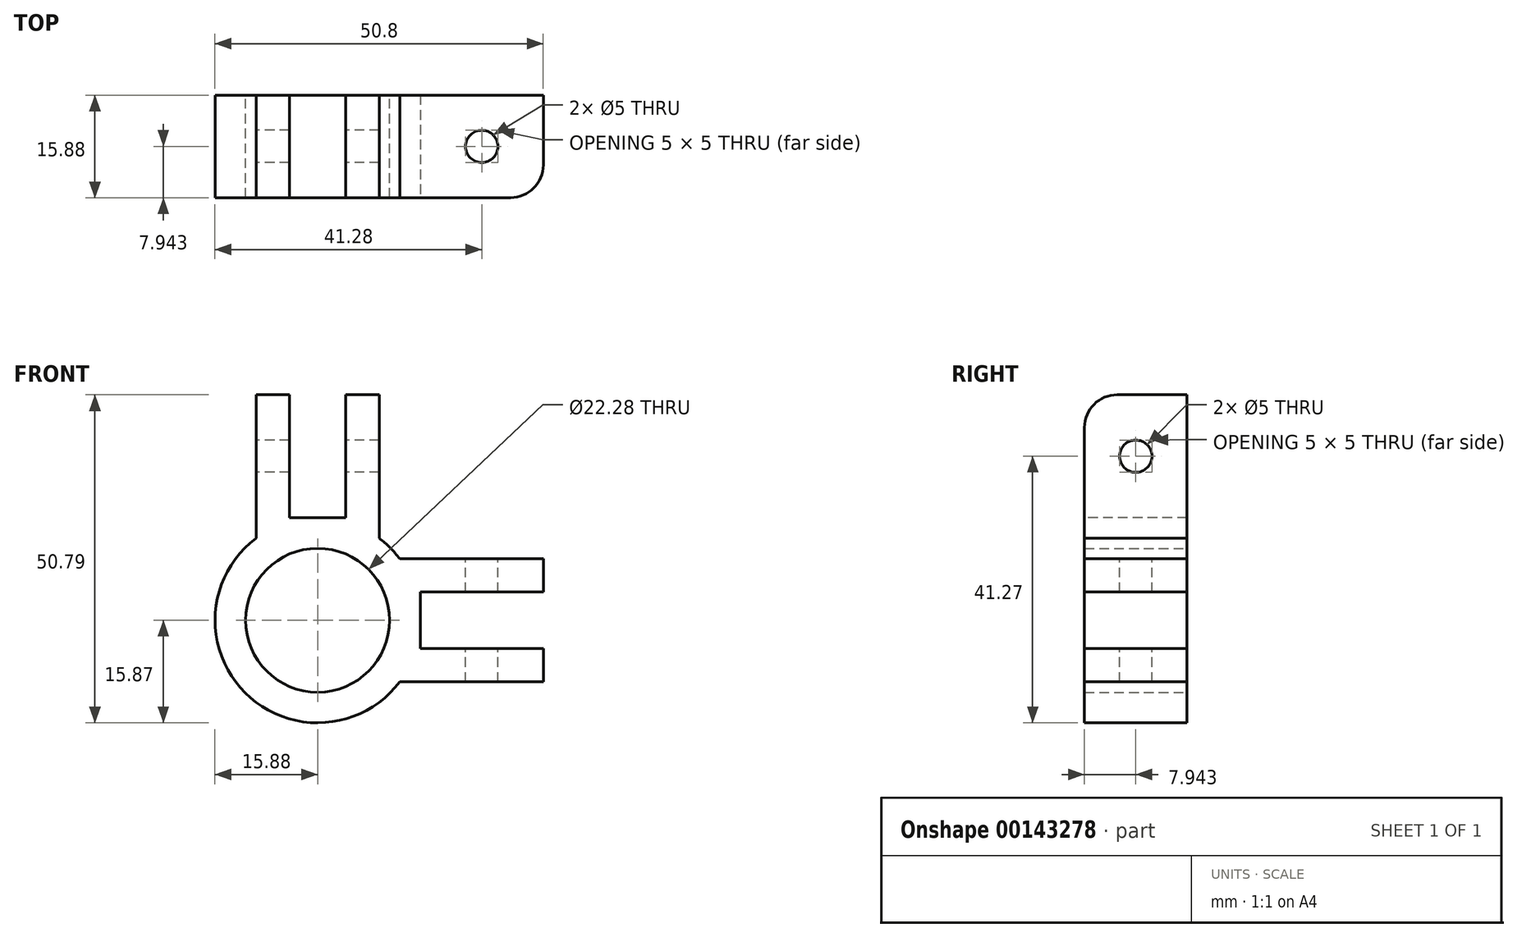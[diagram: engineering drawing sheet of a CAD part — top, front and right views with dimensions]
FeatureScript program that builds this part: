
annotation { "Feature Type Name" : "Feature", "Feature Type Description" : "" }
export const myFeature = defineFeature(function(context is Context, id is Id, definition is map)
    precondition{}
    {
        {
            var Q0;
            Q0=qCreatedBy(makeId("Front.planeOp"),FACE);
            var sketch = newSketch(context, id + "F0", { "sketchPlane" : qUnion([Q0])});
            skCircle(sketch, "E0", {"center": v(0, 0) * mm, "radius": 11.14 * mm});
            skCircle(sketch, "E1", {"center": v(0, 0) * mm, "radius": 15.88 * mm});
            skSolve(sketch);
        }
        {
            var Q0;
            Q0 = qSketchRegion(id + "F0", true);
            extrude(context, id + "F1", {"entities" : qUnion([Q0]), "depth" : 15.88 * mm, "offsetDistance" : 25.4 * mm});
        }
        {
            var Q0;
            Q0=makeQuery(id+"F1.opExtrude","CAP_FACE",FACE,{"disambiguationData":[OSD([sQuery(id+"F0.wireOp",EDGE,"E0"),sQuery(id+"F0.wireOp",EDGE,"E1")])],"isStart":false});
            var sketch = newSketch(context, id + "F2", { "sketchPlane" : qUnion([Q0])});
            skLineSegment(sketch, "E2.bottom", {"start": v(9.52, 34.93) * mm, "end": v(-9.52, 34.93) * mm});
            skPoint(sketch, "E2.middle", {"position": v(0, 0) * mm});
            skCircle(sketch, "E3", {"center": v(0, 0) * mm, "radius": 4.83 * mm});
            skPoint(sketch, "E4.startSnap0", {"position": v(-9.52, 0) * mm});
            skLineSegment(sketch, "E5", {"start": v(0, 11.6) * mm, "end": v(0, -11.6) * mm});
            skLineSegment(sketch, "E6.bottom", {"start": v(4.37, 15.88) * mm, "end": v(-4.37, 15.88) * mm});
            skPoint(sketch, "E6.middle", {"position": v(0, 34.93) * mm});
            skCircle(sketch, "E7", {"center": v(0, 0) * mm, "radius": 9.53 * mm});
            skCircle(sketch, "E8", {"center": v(0, 0) * mm, "radius": 14.37 * mm});
            skLineSegment(sketch, "E9", {"start": v(-9.53, 34.93) * mm, "end": v(-9.53, 12.7) * mm});
            skLineSegment(sketch, "E10", {"start": v(9.52, 34.93) * mm, "end": v(9.52, 12.7) * mm});
            skLineSegment(sketch, "E11", {"start": v(4.37, 15.88) * mm, "end": v(4.37, 34.93) * mm});
            skLineSegment(sketch, "E12", {"start": v(-4.37, 15.88) * mm, "end": v(-4.37, 34.93) * mm});
            skLineSegment(sketch, "E13.1.0", {"start": v(34.92, -9.53) * mm, "end": v(34.92, 9.52) * mm});
            skLineSegment(sketch, "E13.1.1", {"start": v(34.92, 9.53) * mm, "end": v(12.7, 9.53) * mm});
            skLineSegment(sketch, "E13.1.2", {"start": v(15.87, 4.37) * mm, "end": v(34.92, 4.37) * mm});
            skLineSegment(sketch, "E13.1.3", {"start": v(15.87, -4.37) * mm, "end": v(15.87, 4.37) * mm});
            skLineSegment(sketch, "E13.1.4", {"start": v(15.87, -4.37) * mm, "end": v(34.92, -4.37) * mm});
            skLineSegment(sketch, "E13.1.5", {"start": v(34.92, -9.52) * mm, "end": v(12.7, -9.52) * mm});
            skLineSegment(sketch, "E13.anchor1", {"start": v(0, 0) * mm, "end": v(-9.52, 34.93) * mm, "construction": true});
            skLineSegment(sketch, "E13.anchor2", {"start": v(0, 0) * mm, "end": v(34.93, 9.53) * mm, "construction": true});
            skPoint(sketch, "E14", {"position": v(0, 15.88) * mm});
            skLineSegment(sketch, "E15", {"start": v(0, 15.88) * mm, "end": v(0, 11.6) * mm});
            skSolve(sketch);
        }
        {
            var Q0;
            {var subQ1=sQuery(id+"F2.wireOp",EDGE,"E9");Q0=makeQuery(id+"F2.imprint","IMPRINT",FACE,{"disambiguationData":[TD([[makeQuery(id+"F2.imprint","IMPRINT",EDGE,{"derivedFrom":subQ1}),1.0]])]});}
            var Q1;
            {var subQ0=sQuery(id+"F2.wireOp",EDGE,"E10");Q1=makeQuery(id+"F2.imprint","IMPRINT",FACE,{"disambiguationData":[TD([[makeQuery(id+"F2.imprint","IMPRINT",EDGE,{"derivedFrom":subQ0}),-1.0]])]});}
            var Q2;
            {var subQ4=sQuery(id+"F2.wireOp",EDGE,"E13.1.1");Q2=makeQuery(id+"F2.imprint","IMPRINT",FACE,{"disambiguationData":[TD([[makeQuery(id+"F2.imprint","IMPRINT",EDGE,{"derivedFrom":subQ4}),1.0]])]});}
            var Q3;
            {var subQ1=sQuery(id+"F2.wireOp",EDGE,"E13.1.4");Q3=makeQuery(id+"F2.imprint","IMPRINT",FACE,{"disambiguationData":[TD([[makeQuery(id+"F2.imprint","IMPRINT",EDGE,{"derivedFrom":subQ1}),-1.0]])]});}
            var Q4;
            Q4=makeQuery(id+"F1.opExtrude","CAP_FACE",FACE,{"disambiguationData":[OSD([sQuery(id+"F0.wireOp",EDGE,"E0"),sQuery(id+"F0.wireOp",EDGE,"E1")])],"isStart":true});
            extrude(context, id + "F3", {"entities" : qUnion([Q0, Q1, Q2, Q3]), "operationType" : NewBodyOperationType.ADD, "endBound" : BoundingType.UP_TO_SURFACE, "oppositeDirection" : true, "endBoundEntityFace" : qUnion([Q4]), "depth" : 0 * mm, "offsetDistance" : 25.4 * mm});
        }
        {
            var Q0;
            Q0=qCreatedBy(makeId("Front.planeOp"),FACE);
            var sketch = newSketch(context, id + "F4", { "sketchPlane" : qUnion([Q0])});
            skCircle(sketch, "E16", {"center": v(0, 0) * mm, "radius": 11.14 * mm});
            skSolve(sketch);
        }
        {
            var Q0;
            Q0 = qSketchRegion(id + "F4", true);
            extrude(context, id + "F5", {"entities" : qUnion([Q0]), "operationType" : NewBodyOperationType.REMOVE, "endBound" : BoundingType.THROUGH_ALL, "depth" : 25.4 * mm, "offsetDistance" : 25.4 * mm});
        }
        {
            var Q0;
            Q0=makeQuery(id+"F3.opExtrude","SWEPT_FACE",FACE,{"disambiguationData":[OSD([sQuery(id+"F2.wireOp",EDGE,"E13.1.1")])]});
            var sketch = newSketch(context, id + "F6", { "sketchPlane" : qUnion([Q0])});
            skCircle(sketch, "E17", {"center": v(25.4, -7.94) * mm, "radius": 2.5 * mm});
            skLineSegment(sketch, "E18", {"start": v(25.4, -7.94) * mm, "end": v(34.92, -7.94) * mm});
            skPoint(sketch, "E19", {"position": v(23.81, 0) * mm});
            skSolve(sketch);
        }
        {
            var Q0;
            Q0 = qSketchRegion(id + "F6", true);
            extrude(context, id + "F7", {"entities" : qUnion([Q0]), "operationType" : NewBodyOperationType.REMOVE, "endBound" : BoundingType.THROUGH_ALL, "oppositeDirection" : true, "depth" : 25.4 * mm, "offsetDistance" : 25.4 * mm});
        }
        {
            var Q0;
            Q0=makeQuery(id+"F3.opExtrude","SWEPT_FACE",FACE,{"disambiguationData":[OSD([sQuery(id+"F2.wireOp",EDGE,"E9")])]});
            var sketch = newSketch(context, id + "F8", { "sketchPlane" : qUnion([Q0])});
            skPoint(sketch, "E20", {"position": v(7.94, 34.93) * mm});
            skPoint(sketch, "E21", {"position": v(0, 23.81) * mm});
            skLineSegment(sketch, "E22", {"start": v(7.94, 25.4) * mm, "end": v(7.94, 34.93) * mm});
            skCircle(sketch, "E23", {"center": v(7.94, 25.4) * mm, "radius": 2.5 * mm});
            skSolve(sketch);
        }
        {
            var Q0;
            Q0 = qSketchRegion(id + "F8", true);
            extrude(context, id + "F9", {"entities" : qUnion([Q0]), "operationType" : NewBodyOperationType.REMOVE, "endBound" : BoundingType.THROUGH_ALL, "oppositeDirection" : true, "depth" : 25.4 * mm, "offsetDistance" : 25.4 * mm});
        }
        {
            var Q0;
            {var subQ0=sQuery(id+"F2.wireOp",EDGE,"E2.bottom");Q0=makeQuery(id+"F3.opExtrude","TWEAK_EDGE",EDGE,{"derivedFrom":[makeQuery(id+"F1.opExtrude","CAP_FACE",FACE,{"disambiguationData":[OSD([sQuery(id+"F0.wireOp",EDGE,"E0"),sQuery(id+"F0.wireOp",EDGE,"E1")])],"isStart":true}),makeQuery(id+"F2.imprint","IMPRINT",EDGE,{"disambiguationData":[TD([[makeQuery(id+"F2.imprint","INTERSECT",VERTEX,{"derivedFrom":[subQ0,sQuery(id+"F2.wireOp",EDGE,"E10")]}),-1.0]])],"derivedFrom":subQ0})]});}
            var Q1;
            {var subQ0=sQuery(id+"F2.wireOp",EDGE,"E2.bottom");Q1=makeQuery(id+"F3.opExtrude","CAP_EDGE",EDGE,{"disambiguationData":[OSD([subQ0]),TDD([makeQuery(id+"F2.imprint","IMPRINT",EDGE,{"disambiguationData":[TD([[makeQuery(id+"F2.imprint","INTERSECT",VERTEX,{"derivedFrom":[subQ0,sQuery(id+"F2.wireOp",EDGE,"E10")]}),-1.0]])],"derivedFrom":subQ0})])],"isStart":true});}
            var Q2;
            {var subQ0=sQuery(id+"F2.wireOp",EDGE,"E2.bottom");Q2=makeQuery(id+"F3.opExtrude","TWEAK_EDGE",EDGE,{"derivedFrom":[makeQuery(id+"F1.opExtrude","CAP_FACE",FACE,{"disambiguationData":[OSD([sQuery(id+"F0.wireOp",EDGE,"E0"),sQuery(id+"F0.wireOp",EDGE,"E1")])],"isStart":true}),makeQuery(id+"F2.imprint","IMPRINT",EDGE,{"disambiguationData":[TD([[makeQuery(id+"F2.imprint","INTERSECT",VERTEX,{"derivedFrom":[subQ0,sQuery(id+"F2.wireOp",EDGE,"E9")]}),1.0]])],"derivedFrom":subQ0})]});}
            var Q3;
            {var subQ0=sQuery(id+"F2.wireOp",EDGE,"E2.bottom");Q3=makeQuery(id+"F3.opExtrude","CAP_EDGE",EDGE,{"disambiguationData":[OSD([subQ0]),TDD([makeQuery(id+"F2.imprint","IMPRINT",EDGE,{"disambiguationData":[TD([[makeQuery(id+"F2.imprint","INTERSECT",VERTEX,{"derivedFrom":[subQ0,sQuery(id+"F2.wireOp",EDGE,"E9")]}),1.0]])],"derivedFrom":subQ0})])],"isStart":true});}
            var Q4;
            {var subQ0=sQuery(id+"F2.wireOp",EDGE,"E13.1.0");Q4=makeQuery(id+"F3.opExtrude","TWEAK_EDGE",EDGE,{"derivedFrom":[makeQuery(id+"F1.opExtrude","CAP_FACE",FACE,{"disambiguationData":[OSD([sQuery(id+"F0.wireOp",EDGE,"E0"),sQuery(id+"F0.wireOp",EDGE,"E1")])],"isStart":true}),makeQuery(id+"F2.imprint","IMPRINT",EDGE,{"disambiguationData":[TD([[makeQuery(id+"F2.imprint","INTERSECT",VERTEX,{"derivedFrom":[subQ0,sQuery(id+"F2.wireOp",EDGE,"E13.1.1")]}),1.0]])],"derivedFrom":subQ0})]});}
            var Q5;
            {var subQ0=sQuery(id+"F2.wireOp",EDGE,"E13.1.0");Q5=makeQuery(id+"F3.opExtrude","CAP_EDGE",EDGE,{"disambiguationData":[OSD([subQ0]),TDD([makeQuery(id+"F2.imprint","IMPRINT",EDGE,{"disambiguationData":[TD([[makeQuery(id+"F2.imprint","INTERSECT",VERTEX,{"derivedFrom":[subQ0,sQuery(id+"F2.wireOp",EDGE,"E13.1.1")]}),1.0]])],"derivedFrom":subQ0})])],"isStart":true});}
            var Q6;
            {var subQ0=sQuery(id+"F2.wireOp",EDGE,"E13.1.0");Q6=makeQuery(id+"F3.opExtrude","TWEAK_EDGE",EDGE,{"derivedFrom":[makeQuery(id+"F1.opExtrude","CAP_FACE",FACE,{"disambiguationData":[OSD([sQuery(id+"F0.wireOp",EDGE,"E0"),sQuery(id+"F0.wireOp",EDGE,"E1")])],"isStart":true}),makeQuery(id+"F2.imprint","IMPRINT",EDGE,{"disambiguationData":[TD([[makeQuery(id+"F2.imprint","INTERSECT",VERTEX,{"derivedFrom":[subQ0,sQuery(id+"F2.wireOp",EDGE,"E13.1.5")]}),-1.0]])],"derivedFrom":subQ0})]});}
            var Q7;
            {var subQ0=sQuery(id+"F2.wireOp",EDGE,"E13.1.0");Q7=makeQuery(id+"F3.opExtrude","CAP_EDGE",EDGE,{"disambiguationData":[OSD([subQ0]),TDD([makeQuery(id+"F2.imprint","IMPRINT",EDGE,{"disambiguationData":[TD([[makeQuery(id+"F2.imprint","INTERSECT",VERTEX,{"derivedFrom":[subQ0,sQuery(id+"F2.wireOp",EDGE,"E13.1.5")]}),-1.0]])],"derivedFrom":subQ0})])],"isStart":true});}
            fillet(context, id + "F10", {"entities" : qUnion([Q0, Q1, Q2, Q3, Q4, Q5, Q6, Q7]), "radius" : 5.08 * mm, "tangentPropagation" : true, "allowEdgeOverflow" : false});
        }
    });
